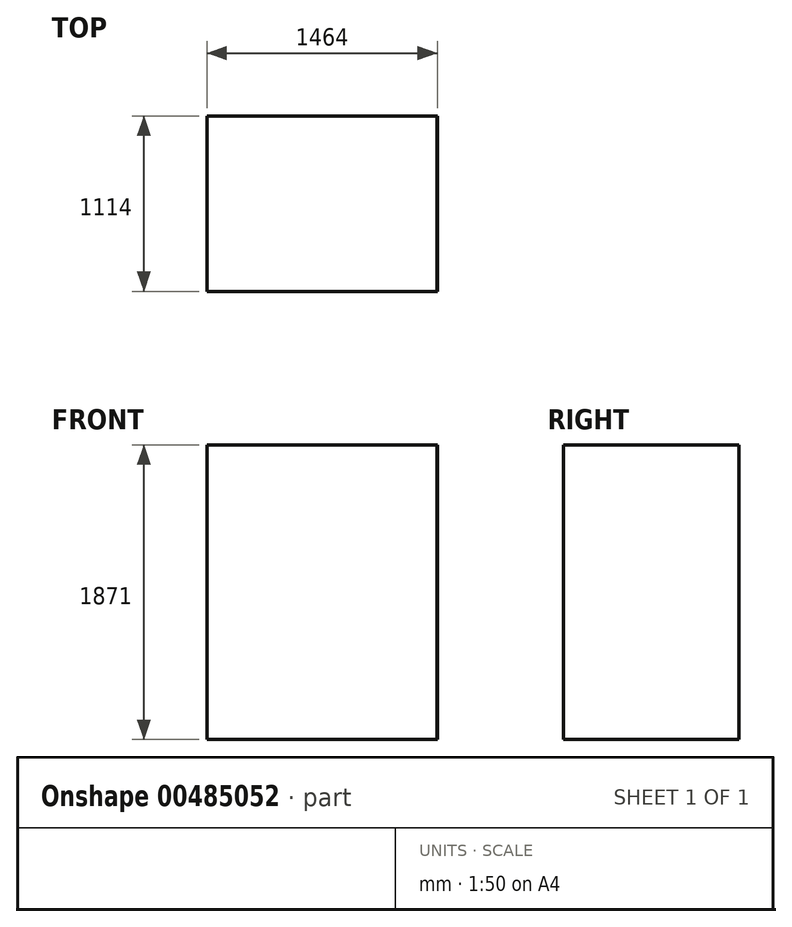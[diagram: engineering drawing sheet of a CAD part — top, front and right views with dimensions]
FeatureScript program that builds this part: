
annotation { "Feature Type Name" : "Feature", "Feature Type Description" : "" }
export const myFeature = defineFeature(function(context is Context, id is Id, definition is map)
    precondition{}
    {
        {
            var Q0;
            Q0=qCreatedBy(makeId("Top.planeOp"),FACE);
            var sketch = newSketch(context, id + "F0", { "sketchPlane" : qUnion([Q0])});
            skLineSegment(sketch, "E0.bottom", {"start": v(732, 557) * mm, "end": v(-732, 557) * mm});
            skLineSegment(sketch, "E0.top", {"start": v(732, -557) * mm, "end": v(-732, -557) * mm});
            skLineSegment(sketch, "E0.left", {"start": v(732, 557) * mm, "end": v(732, -557) * mm});
            skLineSegment(sketch, "E0.right", {"start": v(-732, 557) * mm, "end": v(-732, -557) * mm});
            skPoint(sketch, "E0.middle", {"position": v(0, 0) * mm});
            skSolve(sketch);
        }
        {
            var Q0;
            Q0=qSketchRegion(id+"F0",true);
            extrude(context, id + "F1", {"entities" : qUnion([Q0]), "depth" : 1871 * mm});
        }
        {
            var Q0;
            Q0=makeQuery(id+"F1.opExtrude","CAP_FACE",FACE,{"disambiguationData":[OSD([sQuery(id+"F0.wireOp",EDGE,"E0.bottom"),sQuery(id+"F0.wireOp",EDGE,"E0.top"),sQuery(id+"F0.wireOp",EDGE,"E0.left"),sQuery(id+"F0.wireOp",EDGE,"E0.right")])],"isStart":false});
            var Q1;
            Q1=makeQuery(id+"F1.opExtrude","SWEPT_FACE",FACE,{"disambiguationData":[OSD([sQuery(id+"F0.wireOp",EDGE,"E0.top")])]});
            shell(context, id + "F2", {"entities" : qUnion([Q0, Q1]), "thickness" : 1 * mm});
        }
    });
